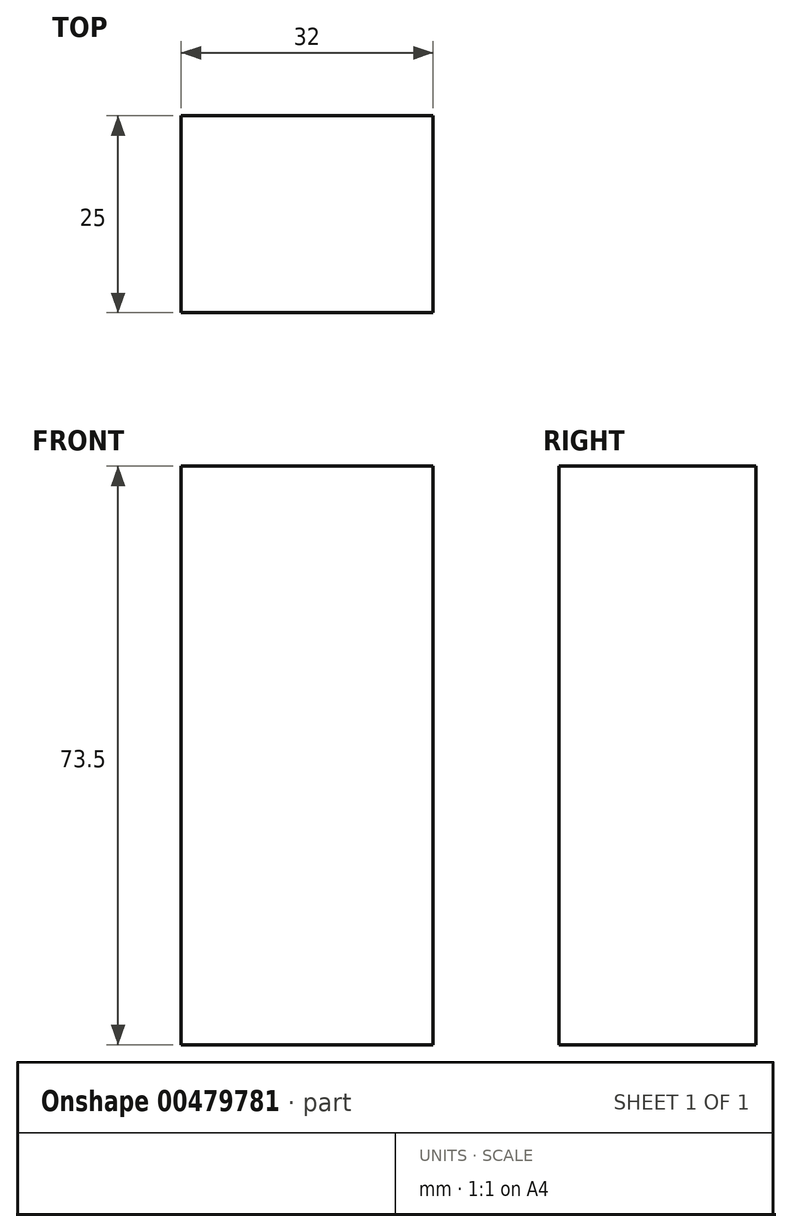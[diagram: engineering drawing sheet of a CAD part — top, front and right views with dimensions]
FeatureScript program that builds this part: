
annotation { "Feature Type Name" : "Feature", "Feature Type Description" : "" }
export const myFeature = defineFeature(function(context is Context, id is Id, definition is map)
    precondition{}
    {
        {
            var Q0;
            Q0=qCreatedBy(makeId("Front.planeOp"),FACE);
            var sketch = newSketch(context, id + "F0", { "sketchPlane" : qUnion([Q0])});
            skLineSegment(sketch, "E0.bottom", {"start": v(0, 0) * mm, "end": v(32, 0) * mm});
            skLineSegment(sketch, "E0.top", {"start": v(0, 73.5) * mm, "end": v(32, 73.5) * mm});
            skLineSegment(sketch, "E0.left", {"start": v(0, 0) * mm, "end": v(0, 73.5) * mm});
            skLineSegment(sketch, "E0.right", {"start": v(32, 0) * mm, "end": v(32, 73.5) * mm});
            skSolve(sketch);
        }
        {
            var Q0;
            Q0=qCreatedBy(makeId("Front.planeOp"),FACE);
            var sketch = newSketch(context, id + "F1", { "sketchPlane" : qUnion([Q0])});
            skLineSegment(sketch, "E1.bottom", {"start": v(15.97, 58.16) * mm, "end": v(19.47, 58.16) * mm});
            skLineSegment(sketch, "E1.top", {"start": v(15.97, 53.66) * mm, "end": v(19.47, 53.66) * mm});
            skLineSegment(sketch, "E1.left", {"start": v(15.97, 58.16) * mm, "end": v(15.97, 53.66) * mm});
            skLineSegment(sketch, "E1.right", {"start": v(19.47, 58.16) * mm, "end": v(19.47, 53.66) * mm});
            skSolve(sketch);
        }
        {
            var Q0;
            Q0=makeQuery(id+"F0.imprint","IMPRINT",FACE,{"disambiguationData":[TD([[makeQuery(id+"F0.imprint","IMPRINT",EDGE,{"derivedFrom":sQuery(id+"F0.wireOp",EDGE,"E0.bottom")}),1.0]])]});
            extrude(context, id + "F2", {"entities" : qUnion([Q0]), "depth" : 25 * mm, "offsetDistance" : 25 * mm});
        }
    });
